# Revit family: LIXIL - 507 N - COBRA MEDICAL BASIN MIXER
name_source: partatom
category: Plumbing Fixtures
units: mm (PartAtom-declared; Revit-internal decimal feet)

## family parameters
Always vertical = Yes
Cut with Voids When Loaded = No
Enable Cutting in Views = No
Maintain Annotation Orientation = No
OmniClass Number = 23.45.00.00
OmniClass Title = Sanitary, Laundry, and Cleaning Equipment
Part Type = Normal
Room Calculation Point = No
Round Connector Dimension = Use Diameter
Shared = Yes
Work Plane-Based = No

## types (1)
- 507 N
    Default Elevation = 0 mm  [stored 0 ft]
    Description = Cobra medical mixer to detail and spec. See sanware schedule. Available from Lixil.
    Hosted on lixil.co.za = https://www.lixil.co.za
    M _ MIXER BODY = M _ LIXIL - CHROME 01
    M _ MIXER INDICATOR 01 = M _ LIXIL - PLASTIC - BLUE 01
    M _ MIXER INDICATOR 02 = M _ LIXIL - PLASTIC - RED 01
    M _ MIXER LEVER = M _ LIXIL - CHROME 01
    M _ MIXER RUBBER = M _ LIXIL - RUBBER - BLACK 01
    Product Specification = Supplier: Lixil.
Product description: Medical elbow-action, progressive control, wall-type mixer, chrome plated. Includes: 1/2 BSP male inlets, aerated underarm swivel outlet (dry spout), and concealed s-connections with integral control stops. Ideal for medical, kitchen & industrial installations. 
Product Code: FEAWALOM-0GT01.
SKU Code: 507/N.
Barcode: 6002194031710.
Brand: Cobra
Range: Medical.
Category: Plumbing Supplies.
Sub-Category: Medical Taps.
Colour: Chrome.
Package Height: 120 mm
Package Width: 210 mm
Package Length: 280 mm
Package Volume: 7056000 mm³
Package Weight: 2.24 kg

Notes:
- Refer to manufacturer's and supplier's installation, maintenance and cleaning manual.
- Refer to manufacturer's and supplier's guarantees and warrantees document.

note: [stored X ft] marks values corroborated as IEEE doubles in the binary element streams (Revit-internal decimal feet)

## geometry (parser evidence)
native form markers: Sweep x10
no freeform markers — native parametric forms only
